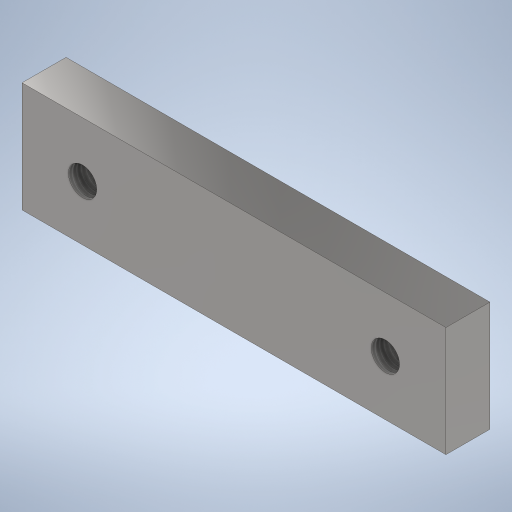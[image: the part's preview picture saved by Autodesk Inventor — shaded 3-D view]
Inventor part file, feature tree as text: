
AUTODESK INVENTOR PART (.ipt)
format: ipt  version: 2023.2 (Build 272271000, 271)  size: 226,816 bytes
history: native  units: mm
features: sketch x2, extrude x1, hole x1
ambient origin geometry x8: Origin, YZ Plane, XZ Plane, XY Plane, X Axis, Y Axis, Z Axis, Center Point
bodies: Solid1 (feature_tree)
feature tree (4):
  extrude  "Extrusion1"  Depth=20.0mm
  hole  "Hole1"  [1 undecoded]
  sketch  "Sketch1"  dims[d0=77.0mm d1=20.0mm]
  sketch  "Sketch2"  dims[d2=8.0mm d3=0.0mm d4=10.0mm d5=10.0mm d6=11.0mm d7=5.133974mm d8=6.0mm d9=11.0mm d10=4.0mm d11=14.3117mm d12=6.0mm d13=0.0mm d14=11.0mm]
note: 1 required parameter value undecoded (feature->parameter linkage not recoverable at this tier; creation-order binding heuristic only, values carry confidence <= 0.55)
